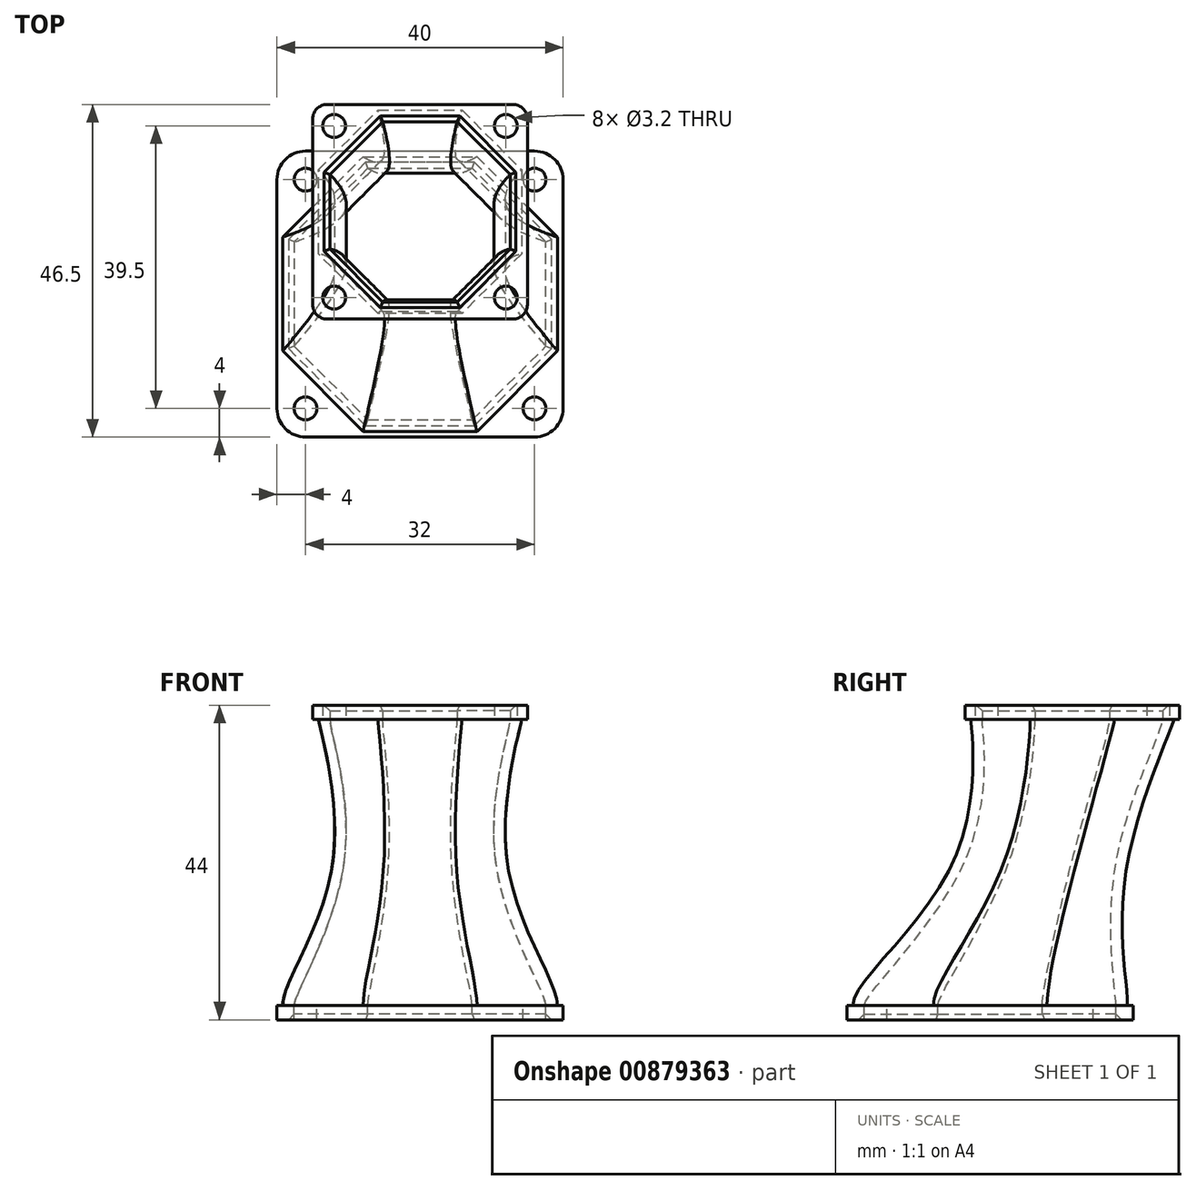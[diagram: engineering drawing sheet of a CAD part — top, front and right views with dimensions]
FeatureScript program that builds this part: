
annotation { "Feature Type Name" : "Feature", "Feature Type Description" : "" }
export const myFeature = defineFeature(function(context is Context, id is Id, definition is map)
    precondition{}
    {
        {
            var Q0;
            Q0=qCreatedBy(makeId("Top.planeOp"),FACE);
            var sketch = newSketch(context, id + "F0", { "sketchPlane" : qUnion([Q0])});
            skLineSegment(sketch, "E0.bottom", {"start": v(-20, -20) * mm, "end": v(20, -20) * mm});
            skLineSegment(sketch, "E0.top", {"start": v(-20, 20) * mm, "end": v(20, 20) * mm});
            skLineSegment(sketch, "E0.left", {"start": v(-20, -20) * mm, "end": v(-20, 20) * mm});
            skLineSegment(sketch, "E0.right", {"start": v(20, -20) * mm, "end": v(20, 20) * mm});
            skPoint(sketch, "E0.middle", {"position": v(0, 0) * mm});
            skLineSegment(sketch, "E1.bottom", {"start": v(-16, -16) * mm, "end": v(16, -16) * mm, "construction": true});
            skLineSegment(sketch, "E1.top", {"start": v(-16, 16) * mm, "end": v(16, 16) * mm, "construction": true});
            skLineSegment(sketch, "E1.left", {"start": v(-16, -16) * mm, "end": v(-16, 16) * mm, "construction": true});
            skLineSegment(sketch, "E1.right", {"start": v(16, -16) * mm, "end": v(16, 16) * mm, "construction": true});
            skCircle(sketch, "E2.cCircle", {"center": v(0, 0) * mm, "radius": 19.2 * mm, "construction": true});
            skLineSegment(sketch, "E2.0", {"start": v(7.95, -19.2) * mm, "end": v(-7.95, -19.2) * mm});
            skLineSegment(sketch, "E2.1", {"start": v(-7.95, -19.2) * mm, "end": v(-19.2, -7.95) * mm});
            skLineSegment(sketch, "E2.2", {"start": v(-19.2, -7.95) * mm, "end": v(-19.2, 7.95) * mm});
            skLineSegment(sketch, "E2.3", {"start": v(-19.2, 7.95) * mm, "end": v(-7.95, 19.2) * mm});
            skLineSegment(sketch, "E2.4", {"start": v(-7.95, 19.2) * mm, "end": v(7.95, 19.2) * mm});
            skLineSegment(sketch, "E2.5", {"start": v(7.95, 19.2) * mm, "end": v(19.2, 7.95) * mm});
            skLineSegment(sketch, "E2.6", {"start": v(19.2, 7.95) * mm, "end": v(19.2, -7.95) * mm});
            skLineSegment(sketch, "E2.7", {"start": v(19.2, -7.95) * mm, "end": v(7.95, -19.2) * mm});
            skPoint(sketch, "E2.0.midPoint", {"position": v(0, -19.2) * mm});
            skSolve(sketch);
        }
        {
            var Q0;
            Q0=qCreatedBy(makeId("Top.planeOp"),FACE);
            cPlane(context, id + "F1", {"entities" : qUnion([Q0]), "cplaneType" : CPlaneType.OFFSET, "offset" : 40 * mm, "width" : 150 * mm, "height" : 150 * mm});
        }
        {
            var Q0;
            Q0=qCreatedBy(id+"F1.planeOp",FACE);
            var sketch = newSketch(context, id + "F2", { "sketchPlane" : qUnion([Q0])});
            skLineSegment(sketch, "E3.bottom", {"start": v(15, -3.5) * mm, "end": v(-15, -3.5) * mm});
            skLineSegment(sketch, "E3.top", {"start": v(15, 26.5) * mm, "end": v(-15, 26.5) * mm});
            skLineSegment(sketch, "E3.left", {"start": v(15, -3.5) * mm, "end": v(15, 26.5) * mm});
            skLineSegment(sketch, "E3.right", {"start": v(-15, -3.5) * mm, "end": v(-15, 26.5) * mm});
            skPoint(sketch, "E3.middle", {"position": v(0, 11.5) * mm});
            skLineSegment(sketch, "E4.bottom", {"start": v(12, -0.5) * mm, "end": v(-12, -0.5) * mm, "construction": true});
            skLineSegment(sketch, "E4.top", {"start": v(12, 23.5) * mm, "end": v(-12, 23.5) * mm, "construction": true});
            skLineSegment(sketch, "E4.left", {"start": v(12, -0.5) * mm, "end": v(12, 23.5) * mm, "construction": true});
            skLineSegment(sketch, "E4.right", {"start": v(-12, -0.5) * mm, "end": v(-12, 23.5) * mm, "construction": true});
            skCircle(sketch, "E5.cCircle", {"center": v(0, 11.5) * mm, "radius": 14.2 * mm, "construction": true});
            skLineSegment(sketch, "E5.0", {"start": v(5.88, -2.7) * mm, "end": v(-5.88, -2.7) * mm});
            skLineSegment(sketch, "E5.1", {"start": v(-5.88, -2.7) * mm, "end": v(-14.2, 5.62) * mm});
            skLineSegment(sketch, "E5.2", {"start": v(-14.2, 5.62) * mm, "end": v(-14.2, 17.38) * mm});
            skLineSegment(sketch, "E5.3", {"start": v(-14.2, 17.38) * mm, "end": v(-5.88, 25.7) * mm});
            skLineSegment(sketch, "E5.4", {"start": v(-5.88, 25.7) * mm, "end": v(5.88, 25.7) * mm});
            skLineSegment(sketch, "E5.5", {"start": v(5.88, 25.7) * mm, "end": v(14.2, 17.38) * mm});
            skLineSegment(sketch, "E5.6", {"start": v(14.2, 17.38) * mm, "end": v(14.2, 5.62) * mm});
            skLineSegment(sketch, "E5.7", {"start": v(14.2, 5.62) * mm, "end": v(5.88, -2.7) * mm});
            skPoint(sketch, "E5.0.midPoint", {"position": v(0, -2.7) * mm});
            skSolve(sketch);
        }
        {
            var Q0;
            Q0=qCreatedBy(makeId("Top.planeOp"),FACE);
            cPlane(context, id + "F3", {"entities" : qUnion([Q0]), "cplaneType" : CPlaneType.OFFSET, "offset" : 20 * mm, "width" : 150 * mm, "height" : 150 * mm});
        }
        {
            var Q0;
            Q0=qCreatedBy(id+"F3.planeOp",FACE);
            var sketch = newSketch(context, id + "F4", { "sketchPlane" : qUnion([Q0])});
            skLineSegment(sketch, "E6.bottom", {"start": v(13, 20) * mm, "end": v(-13, 20) * mm});
            skLineSegment(sketch, "E6.top", {"start": v(13, -6) * mm, "end": v(-13, -6) * mm});
            skLineSegment(sketch, "E6.left", {"start": v(13, 20) * mm, "end": v(13, -6) * mm});
            skLineSegment(sketch, "E6.right", {"start": v(-13, 20) * mm, "end": v(-13, -6) * mm});
            skPoint(sketch, "E6.middle", {"position": v(0, 7) * mm});
            skCircle(sketch, "E7.cCircle", {"center": v(0, 7) * mm, "radius": 12.2 * mm, "construction": true});
            skLineSegment(sketch, "E7.0", {"start": v(5.05, -5.2) * mm, "end": v(-5.05, -5.2) * mm});
            skLineSegment(sketch, "E7.1", {"start": v(-5.05, -5.2) * mm, "end": v(-12.2, 1.95) * mm});
            skLineSegment(sketch, "E7.2", {"start": v(-12.2, 1.95) * mm, "end": v(-12.2, 12.05) * mm});
            skLineSegment(sketch, "E7.3", {"start": v(-12.2, 12.05) * mm, "end": v(-5.05, 19.2) * mm});
            skLineSegment(sketch, "E7.4", {"start": v(-5.05, 19.2) * mm, "end": v(5.05, 19.2) * mm});
            skLineSegment(sketch, "E7.5", {"start": v(5.05, 19.2) * mm, "end": v(12.2, 12.05) * mm});
            skLineSegment(sketch, "E7.6", {"start": v(12.2, 12.05) * mm, "end": v(12.2, 1.95) * mm});
            skLineSegment(sketch, "E7.7", {"start": v(12.2, 1.95) * mm, "end": v(5.05, -5.2) * mm});
            skPoint(sketch, "E7.0.midPoint", {"position": v(0, -5.2) * mm});
            skSolve(sketch);
        }
        {
            var Q0;
            Q0=makeQuery(id+"F0.imprint","IMPRINT",FACE,{"disambiguationData":[TD([[makeQuery(id+"F0.imprint","IMPRINT",EDGE,{"derivedFrom":sQuery(id+"F0.wireOp",EDGE,"E2.0")}),-1.0]])]});
            var Q1;
            Q1=makeQuery(id+"F4.imprint","IMPRINT",FACE,{"disambiguationData":[TD([[makeQuery(id+"F4.imprint","IMPRINT",EDGE,{"derivedFrom":sQuery(id+"F4.wireOp",EDGE,"E7.0")}),-1.0]])]});
            var Q2;
            Q2=makeQuery(id+"F2.imprint","IMPRINT",FACE,{"disambiguationData":[TD([[makeQuery(id+"F2.imprint","IMPRINT",EDGE,{"derivedFrom":sQuery(id+"F2.wireOp",EDGE,"E5.0")}),-1.0]])]});
            loft(context, id + "F5", {"startCondition" : LoftEndDerivativeType.NORMAL_TO_PROFILE, "startMagnitude" : .5, "endCondition" : LoftEndDerivativeType.NORMAL_TO_PROFILE, "endMagnitude" : .1, "sheetProfilesArray" : [{ "sheetProfileEntities" : qUnion([Q0]) }, { "sheetProfileEntities" : qUnion([Q1]) }, { "sheetProfileEntities" : qUnion([Q2]) }]});
        }
        {
            var Q0;
            Q0=makeQuery(id+"F5.opLoft","CAP_FACE",FACE,{"disambiguationData":[OSD([makeQuery(id+"F2.imprint","IMPRINT",FACE,{"disambiguationData":[TD([[makeQuery(id+"F2.imprint","IMPRINT",EDGE,{"derivedFrom":sQuery(id+"F2.wireOp",EDGE,"E5.0")}),-1.0]])]})])],"isStart":true});
            var sketch = newSketch(context, id + "F6", { "sketchPlane" : qUnion([Q0])});
            skLineSegment(sketch, "E8.0", {"start": v(12.6, 16.72) * mm, "end": v(5.22, 24.1) * mm});
            skLineSegment(sketch, "E8.1", {"start": v(12.6, 6.28) * mm, "end": v(12.6, 16.72) * mm});
            skLineSegment(sketch, "E8.2", {"start": v(5.22, 24.1) * mm, "end": v(-5.22, 24.1) * mm});
            skLineSegment(sketch, "E8.3", {"start": v(5.22, -1.1) * mm, "end": v(12.6, 6.28) * mm});
            skLineSegment(sketch, "E8.4", {"start": v(-5.22, 24.1) * mm, "end": v(-12.6, 16.72) * mm});
            skLineSegment(sketch, "E8.5", {"start": v(-12.6, 16.72) * mm, "end": v(-12.6, 6.28) * mm});
            skLineSegment(sketch, "E8.6", {"start": v(-12.6, 6.28) * mm, "end": v(-5.22, -1.1) * mm});
            skLineSegment(sketch, "E8.7", {"start": v(-5.22, -1.1) * mm, "end": v(5.22, -1.1) * mm});
            skSolve(sketch);
        }
        {
            var Q0;
            Q0=qCreatedBy(id+"F3.planeOp",FACE);
            var sketch = newSketch(context, id + "F7", { "sketchPlane" : qUnion([Q0])});
            skLineSegment(sketch, "E9.0", {"start": v(-10.6, 2.6) * mm, "end": v(-10.6, 11.4) * mm});
            skLineSegment(sketch, "E9.1", {"start": v(-4.4, -3.6) * mm, "end": v(-10.6, 2.6) * mm});
            skLineSegment(sketch, "E9.2", {"start": v(-10.6, 11.4) * mm, "end": v(-4.4, 17.6) * mm});
            skLineSegment(sketch, "E9.3", {"start": v(4.4, -3.6) * mm, "end": v(-4.4, -3.6) * mm});
            skLineSegment(sketch, "E9.4", {"start": v(-4.4, 17.6) * mm, "end": v(4.4, 17.6) * mm});
            skLineSegment(sketch, "E9.5", {"start": v(4.4, 17.6) * mm, "end": v(10.6, 11.4) * mm});
            skLineSegment(sketch, "E9.6", {"start": v(10.6, 11.4) * mm, "end": v(10.6, 2.6) * mm});
            skLineSegment(sketch, "E9.7", {"start": v(10.6, 2.6) * mm, "end": v(4.4, -3.6) * mm});
            skSolve(sketch);
        }
        {
            var Q0;
            Q0=makeQuery(id+"F5.opLoft","CAP_FACE",FACE,{"disambiguationData":[OSD([makeQuery(id+"F0.imprint","IMPRINT",FACE,{"disambiguationData":[TD([[makeQuery(id+"F0.imprint","IMPRINT",EDGE,{"derivedFrom":sQuery(id+"F0.wireOp",EDGE,"E2.0")}),-1.0]])]})])],"isStart":true});
            var sketch = newSketch(context, id + "F8", { "sketchPlane" : qUnion([Q0])});
            skLineSegment(sketch, "E10.0", {"start": v(-17.6, 7.3) * mm, "end": v(-7.3, 17.6) * mm});
            skLineSegment(sketch, "E10.1", {"start": v(-17.6, -7.3) * mm, "end": v(-17.6, 7.3) * mm});
            skLineSegment(sketch, "E10.2", {"start": v(-7.3, 17.6) * mm, "end": v(7.3, 17.6) * mm});
            skLineSegment(sketch, "E10.3", {"start": v(-7.3, -17.6) * mm, "end": v(-17.6, -7.3) * mm});
            skLineSegment(sketch, "E10.4", {"start": v(7.3, 17.6) * mm, "end": v(17.6, 7.3) * mm});
            skLineSegment(sketch, "E10.5", {"start": v(17.6, 7.3) * mm, "end": v(17.6, -7.3) * mm});
            skLineSegment(sketch, "E10.6", {"start": v(17.6, -7.3) * mm, "end": v(7.3, -17.6) * mm});
            skLineSegment(sketch, "E10.7", {"start": v(7.3, -17.6) * mm, "end": v(-7.3, -17.6) * mm});
            skSolve(sketch);
        }
        {
            var Q0;
            Q0=makeQuery(id+"F8.imprint","IMPRINT",FACE,{"disambiguationData":[TD([[makeQuery(id+"F8.imprint","IMPRINT",EDGE,{"derivedFrom":sQuery(id+"F8.wireOp",EDGE,"E10.0")}),-1.0]])]});
            var Q1;
            Q1=makeQuery(id+"F7.imprint","IMPRINT",FACE,{"disambiguationData":[TD([[makeQuery(id+"F7.imprint","IMPRINT",EDGE,{"derivedFrom":sQuery(id+"F7.wireOp",EDGE,"E9.0")}),-1.0]])]});
            var Q2;
            Q2=makeQuery(id+"F6.imprint","IMPRINT",FACE,{"disambiguationData":[TD([[makeQuery(id+"F6.imprint","IMPRINT",EDGE,{"derivedFrom":sQuery(id+"F6.wireOp",EDGE,"E8.0")}),1.0]])]});
            loft(context, id + "F9", {"operationType" : NewBodyOperationType.REMOVE, "startCondition" : LoftEndDerivativeType.NORMAL_TO_PROFILE, "startMagnitude" : .25, "endCondition" : LoftEndDerivativeType.NORMAL_TO_PROFILE, "endMagnitude" : .25, "sheetProfilesArray" : [{ "sheetProfileEntities" : qUnion([Q0]) }, { "sheetProfileEntities" : qUnion([Q1]) }, { "sheetProfileEntities" : qUnion([Q2]) }]});
        }
        {
            var Q0;
            Q0=makeQuery(id+"F8.imprint","IMPRINT",FACE,{"disambiguationData":[TD([[makeQuery(id+"F8.imprint","IMPRINT",EDGE,{"derivedFrom":sQuery(id+"F8.wireOp",EDGE,"E10.0")}),1.0]])]});
            var Q1;
            Q1=makeQuery(id+"F0.imprint","IMPRINT",FACE,{"disambiguationData":[TD([[makeQuery(id+"F0.imprint","IMPRINT",EDGE,{"derivedFrom":sQuery(id+"F0.wireOp",EDGE,"E0.bottom")}),1.0]])]});
            extrude(context, id + "F10", {"entities" : qUnion([Q0, Q1]), "operationType" : NewBodyOperationType.ADD, "depth" : 2 * mm, "offsetDistance" : 25 * mm});
        }
        {
            var Q0;
            Q0=makeQuery(id+"F2.imprint","IMPRINT",FACE,{"disambiguationData":[TD([[makeQuery(id+"F2.imprint","IMPRINT",EDGE,{"derivedFrom":sQuery(id+"F2.wireOp",EDGE,"E3.bottom")}),-1.0]])]});
            var Q1;
            Q1=makeQuery(id+"F6.imprint","IMPRINT",FACE,{"disambiguationData":[TD([[makeQuery(id+"F6.imprint","IMPRINT",EDGE,{"derivedFrom":sQuery(id+"F6.wireOp",EDGE,"E8.0")}),-1.0]])]});
            extrude(context, id + "F11", {"entities" : qUnion([Q0, Q1]), "operationType" : NewBodyOperationType.ADD, "depth" : 2 * mm, "offsetDistance" : 25 * mm});
        }
        {
            var Q0;
            Q0=sQuery(id+"F2.wireOp",VERTEX,"E4.bottom.end");
            var Q1;
            Q1=sQuery(id+"F2.wireOp",VERTEX,"E4.bottom.start");
            var Q2;
            Q2=sQuery(id+"F2.wireOp",VERTEX,"E4.top.start");
            var Q3;
            Q3=sQuery(id+"F2.wireOp",VERTEX,"E4.top.end");
            var Q4;
            Q4=makeQuery(id+"F5.opLoft","SWEPT_BODY",BODY,{"disambiguationData":[OSD([makeQuery(id+"F0.imprint","IMPRINT",FACE,{"disambiguationData":[TD([[makeQuery(id+"F0.imprint","IMPRINT",EDGE,{"derivedFrom":sQuery(id+"F0.wireOp",EDGE,"E2.0")}),-1.0]])]}),makeQuery(id+"F2.imprint","IMPRINT",FACE,{"disambiguationData":[TD([[makeQuery(id+"F2.imprint","IMPRINT",EDGE,{"derivedFrom":sQuery(id+"F2.wireOp",EDGE,"E5.0")}),-1.0]])]}),sQuery(id+"F4.wireOp",EDGE,"E7.7")])]});
            hole(context, id + "F12", {"style" : HoleStyle.SIMPLE, "endStyle" : HoleEndStyle.BLIND, "oppositeDirection" : true, "holeDiameter" : 3.2 * mm, "majorDiameter" : 5 * mm, "holeDepth" : 20 * mm, "isTappedThrough" : true, "tappedDepth" : 12 * mm, "tapClearance" : 3, "locations" : qUnion([Q0, Q1, Q2, Q3]), "scope" : qUnion([Q4])});
        }
        {
            var Q0;
            Q0=sQuery(id+"F0.wireOp",VERTEX,"E1.bottom.start");
            var Q1;
            Q1=sQuery(id+"F0.wireOp",VERTEX,"E1.bottom.end");
            var Q2;
            Q2=sQuery(id+"F0.wireOp",VERTEX,"E1.top.end");
            var Q3;
            Q3=sQuery(id+"F0.wireOp",VERTEX,"E1.top.start");
            var Q4;
            Q4=makeQuery(id+"F5.opLoft","SWEPT_BODY",BODY,{"disambiguationData":[OSD([makeQuery(id+"F0.imprint","IMPRINT",FACE,{"disambiguationData":[TD([[makeQuery(id+"F0.imprint","IMPRINT",EDGE,{"derivedFrom":sQuery(id+"F0.wireOp",EDGE,"E2.0")}),-1.0]])]}),makeQuery(id+"F2.imprint","IMPRINT",FACE,{"disambiguationData":[TD([[makeQuery(id+"F2.imprint","IMPRINT",EDGE,{"derivedFrom":sQuery(id+"F2.wireOp",EDGE,"E5.0")}),-1.0]])]}),sQuery(id+"F4.wireOp",EDGE,"E7.7")])]});
            hole(context, id + "F13", {"style" : HoleStyle.SIMPLE, "endStyle" : HoleEndStyle.BLIND, "holeDiameter" : 3.2 * mm, "majorDiameter" : 5 * mm, "holeDepth" : 20 * mm, "isTappedThrough" : true, "tappedDepth" : 12 * mm, "tapClearance" : 3, "locations" : qUnion([Q0, Q1, Q2, Q3]), "scope" : qUnion([Q4])});
        }
        {
            var Q0;
            Q0=makeQuery(id+"F11.opExtrude","SWEPT_EDGE",EDGE,{"disambiguationData":[OSD([sQuery(id+"F2.wireOp",EDGE,"E3.top"),sQuery(id+"F2.wireOp",EDGE,"E3.left")])]});
            var Q1;
            Q1=makeQuery(id+"F11.opExtrude","SWEPT_EDGE",EDGE,{"disambiguationData":[OSD([sQuery(id+"F2.wireOp",EDGE,"E3.top"),sQuery(id+"F2.wireOp",EDGE,"E3.right")])]});
            var Q2;
            Q2=makeQuery(id+"F11.opExtrude","SWEPT_EDGE",EDGE,{"disambiguationData":[OSD([sQuery(id+"F2.wireOp",EDGE,"E3.bottom"),sQuery(id+"F2.wireOp",EDGE,"E3.right")])]});
            var Q3;
            Q3=makeQuery(id+"F11.opExtrude","SWEPT_EDGE",EDGE,{"disambiguationData":[OSD([sQuery(id+"F2.wireOp",EDGE,"E3.bottom"),sQuery(id+"F2.wireOp",EDGE,"E3.left")])]});
            fillet(context, id + "F14", {"entities" : qUnion([Q0, Q1, Q2, Q3]), "radius" : 2 * mm, "tangentPropagation" : true, "allowEdgeOverflow" : false});
        }
        {
            var Q0;
            Q0=makeQuery(id+"F10.opExtrude","SWEPT_EDGE",EDGE,{"disambiguationData":[OSD([sQuery(id+"F0.wireOp",EDGE,"E0.top"),sQuery(id+"F0.wireOp",EDGE,"E0.right")])]});
            var Q1;
            Q1=makeQuery(id+"F10.opExtrude","SWEPT_EDGE",EDGE,{"disambiguationData":[OSD([sQuery(id+"F0.wireOp",EDGE,"E0.bottom"),sQuery(id+"F0.wireOp",EDGE,"E0.right")])]});
            var Q2;
            Q2=makeQuery(id+"F10.opExtrude","SWEPT_EDGE",EDGE,{"disambiguationData":[OSD([sQuery(id+"F0.wireOp",EDGE,"E0.bottom"),sQuery(id+"F0.wireOp",EDGE,"E0.left")])]});
            var Q3;
            Q3=makeQuery(id+"F10.opExtrude","SWEPT_EDGE",EDGE,{"disambiguationData":[OSD([sQuery(id+"F0.wireOp",EDGE,"E0.top"),sQuery(id+"F0.wireOp",EDGE,"E0.left")])]});
            fillet(context, id + "F15", {"entities" : qUnion([Q0, Q1, Q2, Q3]), "radius" : 4 * mm, "tangentPropagation" : true, "allowEdgeOverflow" : false});
        }
        {
            var Q0;
            Q0=makeQuery(id+"F10.opExtrude","CAP_EDGE",EDGE,{"disambiguationData":[OSD([sQuery(id+"F8.wireOp",EDGE,"E10.7")])],"isStart":false});
            var Q1;
            Q1=makeQuery(id+"F10.opExtrude","CAP_EDGE",EDGE,{"disambiguationData":[OSD([sQuery(id+"F8.wireOp",EDGE,"E10.6")])],"isStart":false});
            var Q2;
            Q2=makeQuery(id+"F10.opExtrude","CAP_EDGE",EDGE,{"disambiguationData":[OSD([sQuery(id+"F8.wireOp",EDGE,"E10.5")])],"isStart":false});
            var Q3;
            Q3=makeQuery(id+"F10.opExtrude","CAP_EDGE",EDGE,{"disambiguationData":[OSD([sQuery(id+"F8.wireOp",EDGE,"E10.4")])],"isStart":false});
            var Q4;
            Q4=makeQuery(id+"F10.opExtrude","CAP_EDGE",EDGE,{"disambiguationData":[OSD([sQuery(id+"F8.wireOp",EDGE,"E10.2")])],"isStart":false});
            var Q5;
            Q5=makeQuery(id+"F10.opExtrude","CAP_EDGE",EDGE,{"disambiguationData":[OSD([sQuery(id+"F8.wireOp",EDGE,"E10.0")])],"isStart":false});
            var Q6;
            Q6=makeQuery(id+"F10.opExtrude","CAP_EDGE",EDGE,{"disambiguationData":[OSD([sQuery(id+"F8.wireOp",EDGE,"E10.1")])],"isStart":false});
            var Q7;
            Q7=makeQuery(id+"F10.opExtrude","CAP_EDGE",EDGE,{"disambiguationData":[OSD([sQuery(id+"F8.wireOp",EDGE,"E10.3")])],"isStart":false});
            var Q8;
            Q8=makeQuery(id+"F11.opExtrude","CAP_EDGE",EDGE,{"disambiguationData":[OSD([sQuery(id+"F6.wireOp",EDGE,"E8.2")])],"isStart":false});
            var Q9;
            Q9=makeQuery(id+"F11.opExtrude","CAP_EDGE",EDGE,{"disambiguationData":[OSD([sQuery(id+"F6.wireOp",EDGE,"E8.4")])],"isStart":false});
            var Q10;
            Q10=makeQuery(id+"F11.opExtrude","CAP_EDGE",EDGE,{"disambiguationData":[OSD([sQuery(id+"F6.wireOp",EDGE,"E8.5")])],"isStart":false});
            var Q11;
            Q11=makeQuery(id+"F11.opExtrude","CAP_EDGE",EDGE,{"disambiguationData":[OSD([sQuery(id+"F6.wireOp",EDGE,"E8.6")])],"isStart":false});
            var Q12;
            Q12=makeQuery(id+"F11.opExtrude","CAP_EDGE",EDGE,{"disambiguationData":[OSD([sQuery(id+"F6.wireOp",EDGE,"E8.7")])],"isStart":false});
            var Q13;
            Q13=makeQuery(id+"F11.opExtrude","CAP_EDGE",EDGE,{"disambiguationData":[OSD([sQuery(id+"F6.wireOp",EDGE,"E8.3")])],"isStart":false});
            var Q14;
            Q14=makeQuery(id+"F11.opExtrude","CAP_EDGE",EDGE,{"disambiguationData":[OSD([sQuery(id+"F6.wireOp",EDGE,"E8.1")])],"isStart":false});
            var Q15;
            Q15=makeQuery(id+"F11.opExtrude","CAP_EDGE",EDGE,{"disambiguationData":[OSD([sQuery(id+"F6.wireOp",EDGE,"E8.0")])],"isStart":false});
            chamfer(context, id + "F16", {"entities" : qUnion([Q0, Q1, Q2, Q3, Q4, Q5, Q6, Q7, Q8, Q9, Q10, Q11, Q12, Q13, Q14, Q15]), "width" : .8 * mm, "tangentPropagation" : true});
        }
    });
